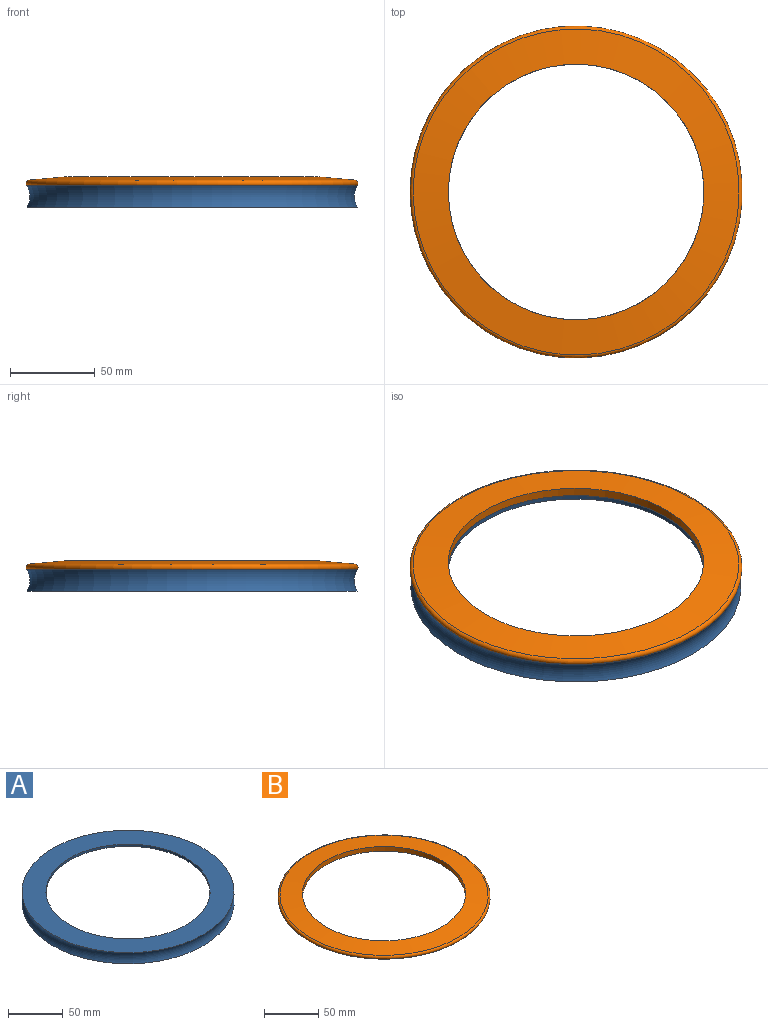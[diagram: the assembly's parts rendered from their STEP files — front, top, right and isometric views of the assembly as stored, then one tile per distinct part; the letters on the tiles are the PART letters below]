
ASSEMBLY  parts=2 mates=1
PART A: 6 faces, bbox 214.7x214.7x17.7 mm
  f0: cylinder r=90.25mm len=180.5mm, axis (0,0,1), area 5670.6mm2, adj f1,f5
  f1: plane 194.5x194.5mm, normal (0,0,-1), area 4123.3mm2, adj f0,f2
  f2: torus R=108.07mm, axis (0,0,1), area 7907.3mm2, adj f1,f3
  f3: plane 194.5x194.5mm, normal (0,0,1), area 11922.3mm2, adj f2,f4
  f4: cylinder r=75.25mm len=150.5mm, axis (0,0,1), area 1182mm2, adj f3,f5
  f5: plane 180.5x180.5mm, normal (0,0,-1), area 7799mm2, adj f0,f4
PART B: 5 faces, bbox 211.8x211.8x5.2 mm
  f0: plane 194.5x194.5mm, normal (0,0,-1), area 11922.3mm2, adj f1,f4
  f1: cylinder r=75.25mm len=150.5mm, axis (0,0,1), area 2458.6mm2, adj f0,f2
  f2: cone r=96.01mm half-angle=85deg, axis (0,0,-1), area 11212.6mm2, adj f1,f3
  f3: torus R=95.84mm, axis (0,0,1), area 2592.5mm2, adj f2,f4
  f4: cone r=97.25mm half-angle=37.7deg, axis (0,0,1), area 155.3mm2, adj f0,f3
PLACE A t=(-24.29,-7.83,3.03)mm fixed
PLACE B rot(axis=(0,0,-1),90deg) t=(-24.29,-7.83,3.03)mm
MATE cylindrical B.f1 <-> A.f0  axis (0,0,-1) through (-24.29,-7.83,15.53)mm
